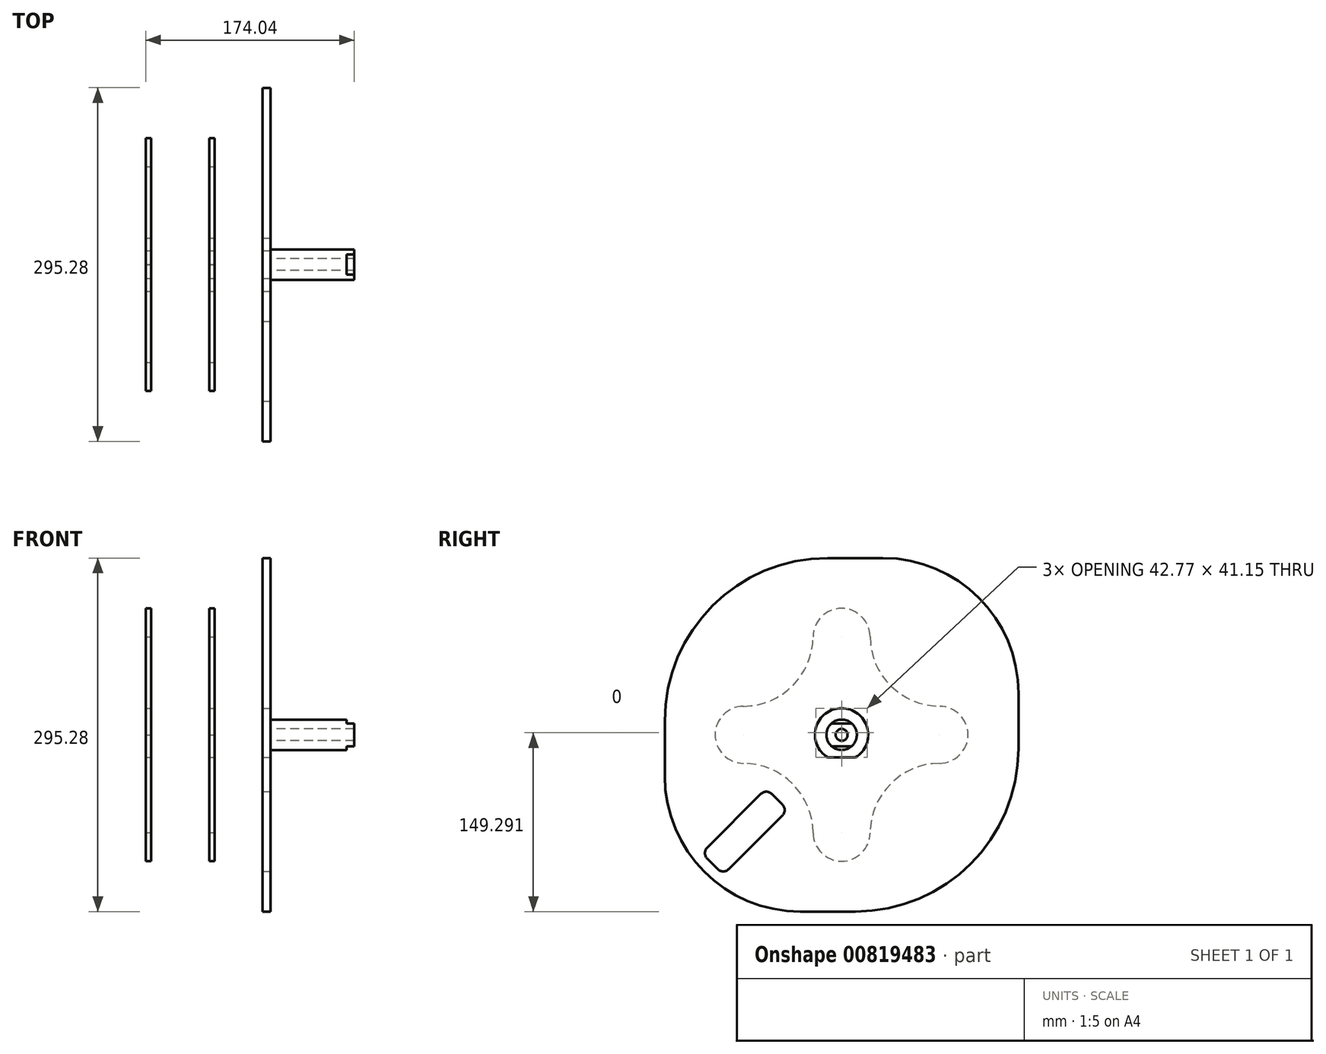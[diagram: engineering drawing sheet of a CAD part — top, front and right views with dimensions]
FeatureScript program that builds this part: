
annotation { "Feature Type Name" : "Feature", "Feature Type Description" : "" }
export const myFeature = defineFeature(function(context is Context, id is Id, definition is map)
    precondition{}
    {
        {
            var Q0;
            Q0=qCreatedBy(makeId("Front.planeOp"),FACE);
            var sketch = newSketch(context, id + "F0", { "sketchPlane" : qUnion([Q0])});
            skLineSegment(sketch, "E0", {"start": v(0, 0) * mm, "end": v(94.66, 0) * mm, "construction": true});
            skLineSegment(sketch, "E1", {"start": v(-109.52, 22.23) * mm, "end": v(0, 22.23) * mm});
            skLineSegment(sketch, "E2", {"start": v(0, 22.23) * mm, "end": v(0, 12.7) * mm});
            skLineSegment(sketch, "E3", {"start": v(0, 12.7) * mm, "end": v(69.85, 12.7) * mm});
            skLineSegment(sketch, "E4", {"start": v(69.85, 12.7) * mm, "end": v(69.85, 0) * mm});
            skLineSegment(sketch, "E5", {"start": v(69.85, 0) * mm, "end": v(-109.52, 0) * mm});
            skLineSegment(sketch, "E6", {"start": v(-109.52, 0) * mm, "end": v(-109.52, 22.23) * mm});
            skLineSegment(sketch, "E7.MirrorCS", {"start": v(0, -12.7) * mm, "end": v(69.85, -12.7) * mm});
            skLineSegment(sketch, "E8.MirrorCS", {"start": v(-109.52, -22.23) * mm, "end": v(0, -22.23) * mm});
            skLineSegment(sketch, "E9.MirrorCS", {"start": v(0, -22.23) * mm, "end": v(0, -12.7) * mm});
            skLineSegment(sketch, "E10.MirrorCS", {"start": v(69.85, -12.7) * mm, "end": v(69.85, 0) * mm});
            skLineSegment(sketch, "E11.MirrorCS", {"start": v(-109.52, 0) * mm, "end": v(-109.52, -22.23) * mm});
            skSolve(sketch);
        }
        {
            var Q0;
            Q0=makeQuery(id+"F0.imprint","IMPRINT",FACE,{"disambiguationData":[TD([[makeQuery(id+"F0.imprint","IMPRINT",EDGE,{"derivedFrom":sQuery(id+"F0.wireOp",EDGE,"E1")}),-1.0]])]});
            var Q1;
            Q1=sQuery(id+"F0.wireOp",EDGE,"E0");
            revolve(context, id + "F1", {"surfaceOperationType" : NewSurfaceOperationType.NEW, "entities" : qUnion([Q0]), "axis" : qUnion([Q1]), "revolveType" : RevolveType.FULL});
        }
        {
            var Q0;
            Q0=makeQuery(id+"F1.opRevolve","SWEPT_FACE",FACE,{"disambiguationData":[OSD([sQuery(id+"F0.wireOp",EDGE,"E6")])]});
            var sketch = newSketch(context, id + "F2", { "sketchPlane" : qUnion([Q0])});
            skArc(sketch, "E12", {"start": v(-2.38, 9.22) * mm, "mid": v(0, -9.53) * mm, "end": v(2.38, 9.22) * mm});
            skLineSegment(sketch, "E13", {"start": v(0, 0) * mm, "end": v(0, 11.6) * mm, "construction": true});
            skLineSegment(sketch, "E14", {"start": v(-2.38, 9.22) * mm, "end": v(-2.38, 11.6) * mm});
            skLineSegment(sketch, "E15", {"start": v(-2.38, 11.6) * mm, "end": v(0, 11.6) * mm});
            skLineSegment(sketch, "E16.MirrorCS", {"start": v(2.38, 11.6) * mm, "end": v(0, 11.6) * mm});
            skLineSegment(sketch, "E17.MirrorCS", {"start": v(2.38, 9.22) * mm, "end": v(2.38, 11.6) * mm});
            skSolve(sketch);
        }
        {
            var Q0;
            Q0 = qSketchRegion(id + "F2", true);
            extrude(context, id + "F3", {"entities" : qUnion([Q0]), "operationType" : NewBodyOperationType.REMOVE, "oppositeDirection" : true, "depth" : 48.26 * mm, "offsetDistance" : 25.4 * mm});
        }
        {
            var Q0;
            Q0=makeQuery(id+"F1.opRevolve","SWEPT_FACE",FACE,{"disambiguationData":[OSD([sQuery(id+"F0.wireOp",EDGE,"E4")])]});
            var sketch = newSketch(context, id + "F4", { "sketchPlane" : qUnion([Q0])});
            skPoint(sketch, "E18", {"position": v(0, 0) * mm});
            skSolve(sketch);
        }
        {
            var Q0;
            Q0=sQuery(id+"F4.wireOp",VERTEX,"E18");
            var Q1;
            Q1=makeQuery(id+"F1.opRevolve","SWEPT_BODY",BODY,{"disambiguationData":[OSD([sQuery(id+"F0.wireOp",EDGE,"E1"),sQuery(id+"F0.wireOp",EDGE,"E2"),sQuery(id+"F0.wireOp",EDGE,"E3"),sQuery(id+"F0.wireOp",EDGE,"E4"),sQuery(id+"F0.wireOp",EDGE,"E6"),sQuery(id+"F0.wireOp",EDGE,"E5")])]});
            hole(context, id + "F5", {"style" : HoleStyle.SIMPLE, "endStyle" : HoleEndStyle.THROUGH, "standardTappedOrClearance" : lookupTablePath({ "standard" : "ANSI", "engagement" : "75%", "pitch" : "20 tpi", "size" : "7/16", "type" : "Tapped" }), "standardBlindInLast" : lookupTablePath({ "standard" : "ANSI", "engagement" : "75%", "pitch" : "20 tpi", "size" : "7/16", "type" : "Tapped" }), "holeDiameter" : 9.92 * mm, "majorDiameter" : 11.1 * mm, "showTappedDepth" : true, "tappedDepth" : 25.4 * mm, "tapClearance" : 3, "locations" : qUnion([Q0]), "scope" : qUnion([Q1]), "startStyle" : HoleStartStyle.SKETCH});
        }
        {
            var Q0;
            Q0=makeQuery(id+"F1.opRevolve","SWEPT_FACE",FACE,{"disambiguationData":[OSD([sQuery(id+"F0.wireOp",EDGE,"E6")])]});
            var sketch = newSketch(context, id + "F6", { "sketchPlane" : qUnion([Q0])});
            skArc(sketch, "E19.0", {"start": v(-11.66, -18.92) * mm, "mid": v(0, -22.22) * mm, "end": v(11.66, -18.92) * mm});
            skLineSegment(sketch, "E20", {"start": v(-11.66, -18.92) * mm, "end": v(11.66, -18.92) * mm});
            skSolve(sketch);
        }
        {
            var Q0;
            Q0 = qSketchRegion(id + "F6", true);
            extrude(context, id + "F7", {"entities" : qUnion([Q0]), "operationType" : NewBodyOperationType.REMOVE, "endBound" : BoundingType.THROUGH_ALL, "oppositeDirection" : true, "depth" : 25.4 * mm, "offsetDistance" : 25.4 * mm});
        }
        {
            var Q0;
            Q0=makeQuery(id+"F1.opRevolve","SWEPT_FACE",FACE,{"disambiguationData":[OSD([sQuery(id+"F0.wireOp",EDGE,"E4")])]});
            var sketch = newSketch(context, id + "F8", { "sketchPlane" : qUnion([Q0])});
            skArc(sketch, "E21.0", {"start": v(-8.4, -9.52) * mm, "mid": v(0, -12.7) * mm, "end": v(8.4, -9.52) * mm});
            skLineSegment(sketch, "E22", {"start": v(-8.4, 9.52) * mm, "end": v(8.4, 9.52) * mm});
            skLineSegment(sketch, "E23", {"start": v(-8.4, -9.53) * mm, "end": v(8.4, -9.53) * mm});
            skArc(sketch, "E24.trimOffspring", {"start": v(8.4, 9.53) * mm, "mid": v(0, 12.7) * mm, "end": v(-8.4, 9.52) * mm});
            skSolve(sketch);
        }
        {
            var Q0;
            Q0 = qSketchRegion(id + "F8", true);
            extrude(context, id + "F9", {"entities" : qUnion([Q0]), "operationType" : NewBodyOperationType.REMOVE, "oppositeDirection" : true, "depth" : 6.35 * mm, "offsetDistance" : 25.4 * mm});
        }
        {
            var Q0;
            Q0=qCreatedBy(makeId("Right.planeOp"),FACE);
            var sketch = newSketch(context, id + "F10", { "sketchPlane" : qUnion([Q0])});
            skLineSegment(sketch, "E25.bottom", {"start": v(34.5, 147.64) * mm, "end": v(-11.5, 147.64) * mm});
            skLineSegment(sketch, "E25.top", {"start": v(11.5, -147.64) * mm, "end": v(-34.5, -147.64) * mm});
            skLineSegment(sketch, "E25.left", {"start": v(147.64, 34.5) * mm, "end": v(147.64, -11.5) * mm});
            skLineSegment(sketch, "E25.right", {"start": v(-147.64, 11.5) * mm, "end": v(-147.64, -34.5) * mm});
            skPoint(sketch, "E25.middle", {"position": v(0, 0) * mm});
            skPoint(sketch, "E26.visualSharp", {"position": v(-147.64, -147.64) * mm});
            skArc(sketch, "E26.filletArc", {"start": v(-147.64, -34.5) * mm, "mid": v(-114.5, -114.5) * mm, "end": v(-34.5, -147.64) * mm});
            skPoint(sketch, "E27.visualSharp", {"position": v(147.64, 147.64) * mm});
            skArc(sketch, "E27.filletArc", {"start": v(147.64, 34.5) * mm, "mid": v(114.5, 114.5) * mm, "end": v(34.5, 147.64) * mm});
            skPoint(sketch, "E28.visualSharp", {"position": v(147.64, -147.64) * mm});
            skArc(sketch, "E28.filletArc", {"start": v(11.5, -147.64) * mm, "mid": v(107.76, -107.76) * mm, "end": v(147.64, -11.5) * mm});
            skPoint(sketch, "E29.visualSharp", {"position": v(-147.64, 147.64) * mm});
            skArc(sketch, "E29.filletArc", {"start": v(-11.5, 147.64) * mm, "mid": v(-107.76, 107.76) * mm, "end": v(-147.64, 11.5) * mm});
            skSolve(sketch);
        }
        {
            var Q0;
            Q0=makeQuery(id+"F10.imprint","IMPRINT",FACE,{"disambiguationData":[TD([[makeQuery(id+"F10.imprint","IMPRINT",EDGE,{"derivedFrom":sQuery(id+"F10.wireOp",EDGE,"E25.bottom")}),1.0]])]});
            var Q1;
            Q1=makeQuery(id+"F1.opRevolve","SWEPT_FACE",FACE,{"disambiguationData":[OSD([sQuery(id+"F0.wireOp",EDGE,"E2")])]});
            extrude(context, id + "F11", {"entities" : qUnion([Q0]), "oppositeDirection" : true, "depth" : 6.73 * mm, "endBoundEntityFace" : qUnion([Q1]), "offsetDistance" : 25.4 * mm});
        }
        {
            var Q0;
            Q0=makeQuery(id+"F11.opExtrude","CAP_FACE",FACE,{"disambiguationData":[OSD([sQuery(id+"F10.wireOp",EDGE,"E25.bottom"),sQuery(id+"F10.wireOp",EDGE,"E25.top"),sQuery(id+"F10.wireOp",EDGE,"E25.left"),sQuery(id+"F10.wireOp",EDGE,"E25.right")])],"isStart":true});
            var sketch = newSketch(context, id + "F12", { "sketchPlane" : qUnion([Q0])});
            skArc(sketch, "E30.0", {"start": v(-11.66, -18.92) * mm, "mid": v(0, 22.23) * mm, "end": v(11.66, -18.92) * mm});
            skLineSegment(sketch, "E30.1", {"start": v(-11.66, -18.92) * mm, "end": v(11.66, -18.92) * mm});
            skSolve(sketch);
        }
        {
            var Q0;
            Q0=makeQuery(id+"F1.opRevolve","SWEPT_FACE",FACE,{"disambiguationData":[OSD([sQuery(id+"F0.wireOp",EDGE,"E6")])]});
            cPlane(context, id + "F13", {"entities" : qUnion([Q0]), "cplaneType" : CPlaneType.OFFSET, "offset" : 5.33 * mm, "oppositeDirection" : true, "width" : 152.4 * mm, "height" : 152.4 * mm});
        }
        {
            var Q0;
            Q0=qCreatedBy(id+"F13.planeOp",FACE);
            var sketch = newSketch(context, id + "F14", { "sketchPlane" : qUnion([Q0])});
            skLineSegment(sketch, "E31", {"start": v(0, 0) * mm, "end": v(0, 81.75) * mm, "construction": true});
            skLineSegment(sketch, "E32", {"start": v(0, 0) * mm, "end": v(-45.43, 45.43) * mm, "construction": true});
            skArc(sketch, "E33", {"start": v(23.81, 81.92) * mm, "mid": v(0, 105.56) * mm, "end": v(-23.81, 81.92) * mm});
            skArc(sketch, "E34", {"start": v(-81.92, 23.81) * mm, "mid": v(-40.95, 40.95) * mm, "end": v(-23.81, 81.92) * mm});
            skArc(sketch, "E35.MirrorC", {"start": v(81.92, 23.81) * mm, "mid": v(40.95, 40.95) * mm, "end": v(23.81, 81.92) * mm});
            skLineSegment(sketch, "E36", {"start": v(0, 0) * mm, "end": v(-139.42, 0) * mm, "construction": true});
            skLineSegment(sketch, "E37", {"start": v(0, 0) * mm, "end": v(35.96, 35.96) * mm, "construction": true});
            skArc(sketch, "E38.MirrorC", {"start": v(-81.92, -23.81) * mm, "mid": v(-105.56, 0) * mm, "end": v(-81.92, 23.81) * mm});
            skArc(sketch, "E39.MirrorC", {"start": v(81.92, 23.81) * mm, "mid": v(105.56, 0) * mm, "end": v(81.92, -23.81) * mm});
            skArc(sketch, "E40.MirrorC", {"start": v(-23.81, -81.92) * mm, "mid": v(0, -105.56) * mm, "end": v(23.81, -81.92) * mm});
            skArc(sketch, "E41.MirrorC", {"start": v(-81.92, -23.81) * mm, "mid": v(-40.95, -40.95) * mm, "end": v(-23.81, -81.92) * mm});
            skArc(sketch, "E42.MirrorC", {"start": v(81.92, -23.81) * mm, "mid": v(40.95, -40.95) * mm, "end": v(23.81, -81.92) * mm});
            skSolve(sketch);
        }
        {
            var Q0;
            Q0 = qSketchRegion(id + "F14", true);
            extrude(context, id + "F15", {"entities" : qUnion([Q0]), "oppositeDirection" : true, "depth" : 4.44 * mm, "offsetDistance" : 25.4 * mm});
        }
        {
            var Q0;
            Q0=sQuery(id+"F14.wireOp",VERTEX,"E31.end");
            var Q1;
            Q1=sQuery(id+"F14.wireOp",VERTEX,"E38.MirrorC.center");
            var Q2;
            Q2=sQuery(id+"F14.wireOp",VERTEX,"E39.MirrorC.center");
            var Q3;
            Q3=sQuery(id+"F14.wireOp",VERTEX,"E40.MirrorC.center");
            var Q4;
            Q4=makeQuery(id+"F15.opExtrude","SWEPT_BODY",BODY,{"disambiguationData":[OSD([sQuery(id+"F14.wireOp",EDGE,"E33"),sQuery(id+"F14.wireOp",EDGE,"E34"),sQuery(id+"F14.wireOp",EDGE,"E35.MirrorC"),sQuery(id+"F14.wireOp",EDGE,"E38.MirrorC"),sQuery(id+"F14.wireOp",EDGE,"E39.MirrorC"),sQuery(id+"F14.wireOp",EDGE,"E40.MirrorC"),sQuery(id+"F14.wireOp",EDGE,"E41.MirrorC"),sQuery(id+"F14.wireOp",EDGE,"E42.MirrorC")])]});
            hole(context, id + "F16", {"style" : HoleStyle.SIMPLE, "endStyle" : HoleEndStyle.THROUGH, "standardTappedOrClearance" : lookupTablePath({ "standard" : "ANSI", "size" : "1/2 (0.5)", "type" : "Drilled" }), "standardBlindInLast" : lookupTablePath({ "standard" : "ANSI", "size" : "1/2", "type" : "Drilled" }), "holeDiameter" : 1 / 50.8 * mm, "majorDiameter" : 11.1 * mm, "tappedDepth" : 25.4 * mm, "tapClearance" : 3, "locations" : qUnion([Q0, Q1, Q2, Q3]), "scope" : qUnion([Q4]), "startStyle" : HoleStartStyle.SKETCH});
        }
        {
            var Q0;
            Q0=makeQuery(id+"F15.opExtrude","SWEPT_BODY",BODY,{"disambiguationData":[OSD([sQuery(id+"F14.wireOp",EDGE,"E33"),sQuery(id+"F14.wireOp",EDGE,"E34"),sQuery(id+"F14.wireOp",EDGE,"E35.MirrorC"),sQuery(id+"F14.wireOp",EDGE,"E38.MirrorC"),sQuery(id+"F14.wireOp",EDGE,"E39.MirrorC"),sQuery(id+"F14.wireOp",EDGE,"E40.MirrorC"),sQuery(id+"F14.wireOp",EDGE,"E41.MirrorC"),sQuery(id+"F14.wireOp",EDGE,"E42.MirrorC")])]});
            transform(context, id + "F17", {"entities" : qUnion([Q0]), "transformType" : TransformType.TRANSLATION_3D, "dx" : 52.96 * mm, "dy" : 0 * mm, "dz" : 0 * mm, "makeCopy" : true});
        }
        {
            var Q0;
            Q0 = qSketchRegion(id + "F12", true);
            var Q1;
            Q1=makeQuery(id+"F11.opExtrude","CAP_FACE",FACE,{"disambiguationData":[OSD([sQuery(id+"F10.wireOp",EDGE,"E25.bottom"),sQuery(id+"F10.wireOp",EDGE,"E25.top"),sQuery(id+"F10.wireOp",EDGE,"E25.left"),sQuery(id+"F10.wireOp",EDGE,"E25.right")])],"isStart":false});
            extrude(context, id + "F18", {"entities" : qUnion([Q0]), "operationType" : NewBodyOperationType.REMOVE, "endBound" : BoundingType.THROUGH_ALL, "oppositeDirection" : true, "depth" : 25.4 * mm, "endBoundEntityFace" : qUnion([Q1]), "offsetDistance" : 25.4 * mm});
        }
        {
            var Q0;
            Q0=makeQuery(id+"F11.opExtrude","CAP_FACE",FACE,{"disambiguationData":[OSD([sQuery(id+"F10.wireOp",EDGE,"E25.bottom"),sQuery(id+"F10.wireOp",EDGE,"E25.top"),sQuery(id+"F10.wireOp",EDGE,"E25.left"),sQuery(id+"F10.wireOp",EDGE,"E25.right"),sQuery(id+"F10.wireOp",EDGE,"E26.filletArc"),sQuery(id+"F10.wireOp",EDGE,"E27.filletArc"),sQuery(id+"F10.wireOp",EDGE,"E28.filletArc"),sQuery(id+"F10.wireOp",EDGE,"E29.filletArc")])],"isStart":true});
            var sketch = newSketch(context, id + "F19", { "sketchPlane" : qUnion([Q0])});
            skLineSegment(sketch, "E43", {"start": v(0, 0) * mm, "end": v(-80.82, -80.82) * mm, "construction": true});
            skLineSegment(sketch, "E44", {"start": v(0, 0) * mm, "end": v(-113.76, 0) * mm, "construction": true});
            skLineSegment(sketch, "E45.bottom", {"start": v(-67.35, -49.4) * mm, "end": v(-112.25, -94.3) * mm});
            skLineSegment(sketch, "E45.top", {"start": v(-49.4, -67.35) * mm, "end": v(-94.3, -112.25) * mm});
            skLineSegment(sketch, "E45.left", {"start": v(-58.37, -49.4) * mm, "end": v(-49.4, -58.37) * mm});
            skLineSegment(sketch, "E45.right", {"start": v(-112.25, -103.27) * mm, "end": v(-103.27, -112.25) * mm});
            skPoint(sketch, "E45.middle", {"position": v(-80.82, -80.82) * mm});
            skPoint(sketch, "E46.visualSharp", {"position": v(-116.74, -98.78) * mm});
            skArc(sketch, "E46.filletArc", {"start": v(-112.25, -94.3) * mm, "mid": v(-114.11, -98.78) * mm, "end": v(-112.25, -103.27) * mm});
            skPoint(sketch, "E47.visualSharp", {"position": v(-98.78, -116.74) * mm});
            skArc(sketch, "E47.filletArc", {"start": v(-103.27, -112.25) * mm, "mid": v(-98.78, -114.11) * mm, "end": v(-94.3, -112.25) * mm});
            skPoint(sketch, "E48.visualSharp", {"position": v(-44.9, -62.86) * mm});
            skArc(sketch, "E48.filletArc", {"start": v(-49.4, -67.35) * mm, "mid": v(-47.53, -62.86) * mm, "end": v(-49.4, -58.37) * mm});
            skPoint(sketch, "E49.visualSharp", {"position": v(-62.86, -44.9) * mm});
            skArc(sketch, "E49.filletArc", {"start": v(-58.37, -49.4) * mm, "mid": v(-62.86, -47.53) * mm, "end": v(-67.35, -49.4) * mm});
            skSolve(sketch);
        }
        {
            var Q0;
            Q0 = qSketchRegion(id + "F19", true);
            extrude(context, id + "F20", {"entities" : qUnion([Q0]), "operationType" : NewBodyOperationType.REMOVE, "endBound" : BoundingType.THROUGH_ALL, "oppositeDirection" : true, "depth" : 25.4 * mm, "offsetDistance" : 25.4 * mm});
        }
    });
